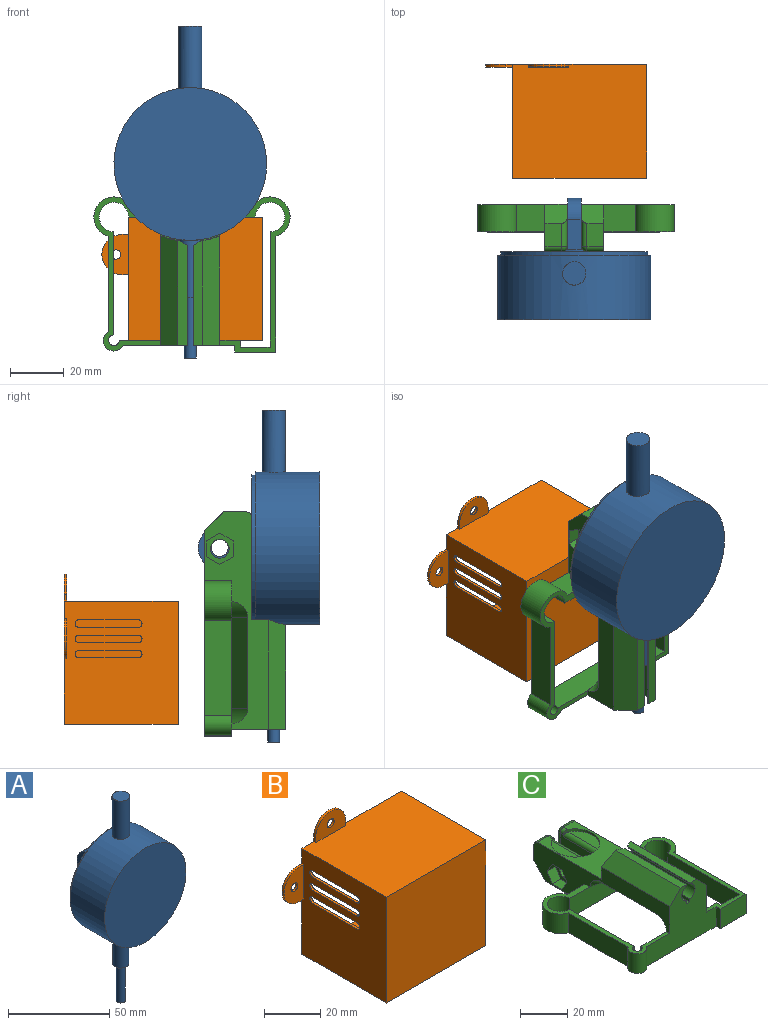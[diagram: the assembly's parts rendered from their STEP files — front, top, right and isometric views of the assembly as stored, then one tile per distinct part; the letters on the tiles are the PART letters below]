
ASSEMBLY  parts=3 mates=2
PART A: 31 faces, bbox 57x45.3x123.9 mm
  f0: cylinder r=28.5mm len=57mm, axis (0,1,0), area 4187.4mm2, adj f11,f12,f13,f15
  f1: plane 19x15.8mm, normal (1,0,0), area 242.2mm2, adj f3,f5,f6,f7,f8
  f2: plane 19x15.8mm, normal (-1,0,0), area 242.2mm2, adj f3,f5,f6,f7,f8
  f3: plane 20x20mm, normal (0,1,0), area 235.2mm2, adj f1,f2,f4,f5,f6
  f4: cylinder r=10mm len=20mm, axis (0,-1,0), area 62.8mm2, adj f3,f10
  f5: plane 11.1x5mm, normal (0,0,-1), area 55.5mm2, adj f1,f2,f3,f7
  f6: plane 11.1x5mm, normal (0,0,1), area 55.5mm2, adj f1,f2,f3,f7
  f7: cylinder r=7.9mm len=15.8mm, axis (1,0,0), area 124.1mm2, adj f1,f2,f5,f6
  f8: cylinder r=3.15mm len=6.3mm, axis (1,0,0), area 99mm2, adj f1,f2
  f9: cylinder r=27.4mm len=54.8mm, axis (0,1,0), area 223.8mm2, adj f10,f12
  f10: plane 54.8x54.8mm, normal (0,1,0), area 1980.8mm2, adj f4,f9,f21,f24,f27,f30
  f11: plane 57x57mm, normal (0,-1,0), area 2551.8mm2, adj f0
  f12: plane 57x57mm, normal (0,1,0), area 193.2mm2, adj f0,f9
  f13: cylinder r=4.35mm len=23.33mm, axis (0,0,-1), area 633.2mm2, adj f0,f14
  f14: plane 8.7x8.7mm, normal (0,0,1), area 59.4mm2, adj f13
  f15: cylinder r=4mm len=21.78mm, axis (0,0,1), area 543.9mm2, adj f0,f16
  f16: plane 8x8mm, normal (0,0,-1), area 35.1mm2, adj f15,f17
  f17: cylinder r=2.2mm len=22.4mm, axis (0,0,1), area 309.6mm2, adj f16,f18
  f18: plane 4.4x4.4mm, normal (0,0,-1), area 15.2mm2, adj f17
  f19: cone r=0mm half-angle=59deg, axis (0,1,0), area 3.7mm2, adj f20
  f20: cylinder r=1mm len=2mm, axis (0,1,0), area 4.7mm2, adj f19,f21
  f21: cone r=1mm half-angle=45deg, axis (0,1,0), area 18mm2, adj f10,f20
  f22: cone r=0mm half-angle=59deg, axis (0,1,0), area 3.7mm2, adj f23
  f23: cylinder r=1mm len=2mm, axis (0,1,0), area 4.7mm2, adj f22,f24
  f24: cone r=1mm half-angle=45deg, axis (0,1,0), area 18mm2, adj f10,f23
  f25: cone r=0mm half-angle=59deg, axis (0,1,0), area 3.7mm2, adj f26
  f26: cylinder r=1mm len=2mm, axis (0,1,0), area 4.7mm2, adj f25,f27
  f27: cone r=1mm half-angle=45deg, axis (0,1,0), area 18mm2, adj f10,f26
  f28: cone r=0mm half-angle=59deg, axis (0,1,0), area 3.7mm2, adj f29
  f29: cylinder r=1mm len=2mm, axis (0,1,0), area 4.7mm2, adj f28,f30
  f30: cone r=1mm half-angle=45deg, axis (0,1,0), area 18mm2, adj f10,f29
PART B: 33 faces, bbox 60x42.5x56 mm
  f0: plane 46x42.5mm, normal (-1,0,0), area 1735mm2, adj f1,f3,f4,f5,f11,f12,f15,f21
  f1: plane 50x42.5mm, normal (0,0,-1), area 2125mm2, adj f0,f2,f4,f5
  f2: plane 46x42.5mm, normal (1,0,0), area 1955mm2, adj f1,f3,f4,f5
  f3: plane 50x42.5mm, normal (0,0,1), area 2110mm2, adj f0,f2,f4,f5,f7,f9,f10
  f4: plane 50x46mm, normal (0,-1,0), area 2300mm2, adj f0,f1,f2,f3
  f5: plane 60x56mm, normal (0,1,0), area 420.5mm2, adj f0,f1,f2,f3,f6,f7,f8,f9
  f6: cylinder r=7.5mm len=15mm, axis (0,1,0), area 23.6mm2, adj f5,f7,f9,f10
  f7: plane 2.5x1mm, normal (-1,0,0), area 2.5mm2, adj f3,f5,f6,f10
  f8: cylinder r=1.75mm len=3.5mm, axis (0,1,0), area 11mm2, adj f5,f10
  f9: plane 2.5x1mm, normal (1,0,0), area 2.5mm2, adj f3,f5,f6,f10
  f10: plane 15x10mm, normal (0,-1,0), area 116.2mm2, adj f3,f6,f7,f8,f9
  f11: plane 2.5x1mm, normal (0,0,-1), area 2.5mm2, adj f0,f5,f13,f15
  f12: plane 2.5x1mm, normal (0,0,1), area 2.5mm2, adj f0,f5,f13,f15
  f13: cylinder r=7.5mm len=15mm, axis (0,1,0), area 23.6mm2, adj f5,f11,f12,f15
  f14: cylinder r=1.75mm len=3.5mm, axis (0,1,0), area 11mm2, adj f5,f15
  f15: plane 15x10mm, normal (0,-1,0), area 116.2mm2, adj f0,f11,f12,f13,f14
  f16: plane 44x41.5mm, normal (1,0,0), area 1621mm2, adj f5,f17,f19,f20,f21,f22,f23,f24
  f17: plane 48x41.5mm, normal (0,0,1), area 1992mm2, adj f5,f16,f18,f20
  f18: plane 44x41.5mm, normal (-1,0,0), area 1826mm2, adj f5,f17,f19,f20
  f19: plane 48x41.5mm, normal (0,0,-1), area 1992mm2, adj f5,f16,f18,f20
  f20: plane 48x44mm, normal (0,1,0), area 2112mm2, adj f16,f17,f18,f19
  f21: cylinder r=1.4mm len=2.8mm, axis (-1,0,0), area 4.4mm2, adj f0,f16,f22,f23
  f22: plane 22.2x1mm, normal (0,0,1), area 22.2mm2, adj f0,f16,f21,f24
  f23: plane 22.2x1mm, normal (0,0,-1), area 22.2mm2, adj f0,f16,f21,f24
  f24: cylinder r=1.4mm len=2.8mm, axis (-1,0,0), area 4.4mm2, adj f0,f16,f22,f23
  f25: cylinder r=1.4mm len=2.8mm, axis (-1,0,0), area 4.4mm2, adj f0,f16,f26,f27
  f26: plane 22.2x1mm, normal (0,0,1), area 22.2mm2, adj f0,f16,f25,f28
  f27: plane 22.2x1mm, normal (0,0,-1), area 22.2mm2, adj f0,f16,f25,f28
  f28: cylinder r=1.4mm len=2.8mm, axis (-1,0,0), area 4.4mm2, adj f0,f16,f26,f27
  f29: cylinder r=1.4mm len=2.8mm, axis (-1,0,0), area 4.4mm2, adj f0,f16,f30,f31
  f30: plane 22.2x1mm, normal (0,0,1), area 22.2mm2, adj f0,f16,f29,f32
  f31: plane 22.2x1mm, normal (0,0,-1), area 22.2mm2, adj f0,f16,f29,f32
  f32: cylinder r=1.4mm len=2.8mm, axis (-1,0,0), area 4.4mm2, adj f0,f16,f30,f31
PART C: 76 faces, bbox 76.5x86.9x34.9 mm
  f0: plane 39.62x4.22mm, normal (0,0,1), area 140.9mm2, adj f19,f47,f53,f57,f68
  f1: cylinder r=4mm len=36.74mm, axis (0,-1,0), area 387.4mm2, adj f19,f57,f66,f68
  f2: plane 18.33x5.6mm, normal (0,0,1), area 73.3mm2, adj f48,f64
  f3: plane 2.03x0.05mm, normal (0,0,1), area 0.1mm2, adj f48,f63
  f4: cylinder r=6mm len=11.77mm, axis (0.83,0,-0.55), area 45.5mm2, adj f5,f15,f55
  f5: plane 49.28x25.27mm, normal (0,0,-1), area 239.5mm2, adj f4,f7,f10,f15,f27,f31,f55,f56
  f6: plane 57.5x25mm, normal (0,0,1), area 221.4mm2, adj f15,f18,f19,f24,f25,f27,f28,f29
  f7: cylinder r=6mm len=11.77mm, axis (-0.83,0,-0.55), area 45.5mm2, adj f5,f10,f56
  f8: plane 57.91x26.25mm, normal (0,0,1), area 229.9mm2, adj f10,f17,f19,f20,f21,f22,f23,f26
  f9: plane 14.46x5.4mm, normal (0,1,0), area 78.1mm2, adj f12,f13,f36,f63
  f10: plane 82.6x25.49mm, normal (1,0,0), area 856.4mm2, adj f5,f7,f8,f11,f17,f19,f36,f38
  f11: plane 8.66x6.3mm, normal (0,1,0), area 54.5mm2, adj f10,f51,f59,f70
  f12: plane 20x15.66mm, normal (-1,0,0), area 240.3mm2, adj f9,f36,f38,f48,f51,f59,f64,f72
  f13: plane 20x15.66mm, normal (1,0,0), area 240.3mm2, adj f9,f16,f36,f48,f52,f58,f62,f75
  f14: plane 8.66x6.3mm, normal (0,1,0), area 54.5mm2, adj f15,f52,f58,f73
  f15: plane 82.6x25.49mm, normal (-1,0,0), area 804.8mm2, adj f4,f5,f6,f14,f19,f24,f36,f39
  f16: cylinder r=3.5mm len=7mm, axis (-1,0,0), area 72.6mm2, adj f13,f45
  f17: plane 11.83x10.16mm, normal (0,1,0), area 120.2mm2, adj f8,f10,f23,f36
  f18: cylinder r=4mm len=10.16mm, axis (0,0,-1), area 147.7mm2, adj f6,f19,f35,f36
  f19: plane 41.54x30.36mm, normal (0,-1,0), area 771.9mm2, adj f0,f1,f6,f8,f10,f15,f18,f20
  f20: plane 10.16x2.5mm, normal (-1,0,0), area 25.4mm2, adj f8,f19,f21,f36
  f21: plane 15.39x10.16mm, normal (0,-1,0), area 156.3mm2, adj f8,f20,f22,f36
  f22: plane 43.23x10.16mm, normal (1,0,0), area 439.2mm2, adj f8,f21,f23,f36
  f23: cylinder r=7.5mm len=14.67mm, axis (0,0,-1), area 306.2mm2, adj f8,f17,f22,f36
  f24: plane 10.58x10.16mm, normal (0,1,0), area 107.5mm2, adj f6,f15,f25,f36
  f25: cylinder r=7.5mm len=14.67mm, axis (0,0,-1), area 306.2mm2, adj f6,f24,f35,f36
  f26: plane 10.16x2.5mm, normal (1,0,0), area 25.4mm2, adj f8,f27,f34,f36
  f27: plane 45.25x10.16mm, normal (0,1,0), area 459.6mm2, adj f5,f6,f8,f26,f28,f36
  f28: cylinder r=2mm len=10.16mm, axis (0,0,-1), area 95.7mm2, adj f6,f27,f29,f36
  f29: plane 38.5x10.16mm, normal (1,0,0), area 391.1mm2, adj f6,f28,f30,f36
  f30: cylinder r=5.5mm len=11mm, axis (0,0,-1), area 263.3mm2, adj f6,f29,f31,f36
  f31: plane 47.25x10.16mm, normal (0,-1,0), area 480mm2, adj f5,f6,f8,f30,f32,f36
  f32: cylinder r=5.5mm len=11mm, axis (0,0,-1), area 263.3mm2, adj f8,f31,f33,f36
  f33: plane 43x10.16mm, normal (-1,0,0), area 436.8mm2, adj f8,f32,f34,f36
  f34: plane 11x10.16mm, normal (0,1,0), area 111.7mm2, adj f8,f26,f33,f36
  f35: plane 35.49x10.16mm, normal (-1,0,0), area 360.5mm2, adj f6,f18,f25,f36
  f36: plane 76.65x73.25mm, normal (0,0,-1), area 989.6mm2, adj f9,f10,f12,f13,f15,f17,f18,f19
  f37: plane 39.62x4.22mm, normal (0,0,1), area 140.9mm2, adj f19,f47,f54,f57,f69
  f38: cylinder r=3.5mm len=8.3mm, axis (-1,0,0), area 182.5mm2, adj f10,f12
  f39: plane 5.1x5mm, normal (0,0.87,0.5), area 29.4mm2, adj f15,f40,f44,f45
  f40: plane 5.1x5mm, normal (0,0.87,-0.5), area 29.4mm2, adj f15,f39,f41,f45
  f41: plane 5.89x5mm, normal (0,0,-1), area 29.4mm2, adj f15,f40,f42,f45
  f42: plane 5.1x5mm, normal (0,-0.87,-0.5), area 29.4mm2, adj f15,f41,f43,f45
  f43: plane 5.1x5mm, normal (0,-0.87,0.5), area 29.4mm2, adj f15,f42,f44,f45
  f44: plane 5.89x5mm, normal (0,0,1), area 29.4mm2, adj f15,f39,f43,f45
  f45: plane 11.78x10.2mm, normal (-1,0,0), area 51.6mm2, adj f16,f39,f40,f41,f42,f43,f44
  f46: plane 40.45x22mm, normal (0,0,1), area 523.7mm2, adj f10,f15,f47,f48,f70,f72,f73,f75
  f47: cylinder r=28.7mm len=22mm, axis (0,0,-1), area 146.1mm2, adj f0,f10,f15,f37,f46,f53,f54,f57
  f48: cylinder r=10.3mm len=20.6mm, axis (0,0,1), area 71.7mm2, adj f2,f3,f12,f13,f46,f49,f62,f63
  f49: plane 18.33x5.6mm, normal (0,0,1), area 73.3mm2, adj f48,f62
  f50: cylinder r=4mm len=36.74mm, axis (0,-1,0), area 387.4mm2, adj f19,f57,f67,f69
  f51: plane 9.14x7.84mm, normal (0,0.71,-0.71), area 81mm2, adj f10,f11,f12,f36,f59
  f52: plane 9.14x7.84mm, normal (0,0.71,-0.71), area 81mm2, adj f13,f14,f15,f36,f58
  f53: plane 41x6.43mm, normal (-0.71,0,0.71), area 356.3mm2, adj f0,f15,f19,f47
  f54: plane 41x6.43mm, normal (0.71,0,0.71), area 356.3mm2, adj f10,f19,f37,f47
  f55: plane 34x9mm, normal (-0.55,0,-0.83), area 367.8mm2, adj f4,f5,f15,f61
  f56: plane 34x9mm, normal (0.55,0,-0.83), area 367.8mm2, adj f5,f7,f10,f60
  f57: bspline ~11.84x11.21mm, area 67.5mm2, adj f0,f1,f37,f47,f50,f65,f66,f67
  f58: cylinder r=2mm len=10.66mm, axis (0,0,1), area 30.3mm2, adj f13,f14,f52,f74
  f59: cylinder r=2mm len=10.66mm, axis (0,0,-1), area 30.3mm2, adj f11,f12,f51,f71
  f60: cylinder r=6mm len=11.77mm, axis (-0.83,0,-0.55), area 45.5mm2, adj f5,f10,f56
  f61: cylinder r=6mm len=11.77mm, axis (0.83,0,-0.55), area 45.5mm2, adj f5,f15,f55
  f62: cylinder r=2mm len=19.45mm, axis (0,-1,0), area 58.3mm2, adj f13,f48,f49,f63
  f63: cylinder r=2mm len=7.92mm, axis (1,0,0), area 19.6mm2, adj f3,f9,f48,f62,f64
  f64: cylinder r=2mm len=19.45mm, axis (0,1,0), area 58.3mm2, adj f2,f12,f48,f63
  f65: plane 38.56x2.29mm, normal (0,0,1), area 76.4mm2, adj f19,f57,f66,f67
  f66: plane 38.31x1.62mm, normal (1,0,0), area 59.1mm2, adj f1,f19,f57,f65
  f67: plane 38.31x1.62mm, normal (-1,0,0), area 59.1mm2, adj f19,f50,f57,f65
  f68: plane 37.4x0.69mm, normal (1,0,0), area 25.1mm2, adj f0,f1,f19,f57
  f69: plane 37.4x0.69mm, normal (-1,0,0), area 25.2mm2, adj f19,f37,f50,f57
  f70: cylinder r=2mm len=6.3mm, axis (1,0,0), area 19.8mm2, adj f10,f11,f46,f71
  f71: sphere r=2mm, area 8.6mm2, adj f59,f70,f72
  f72: cylinder r=2mm len=2.59mm, axis (0,1,0), area 6.9mm2, adj f12,f46,f48,f71
  f73: cylinder r=2mm len=6.3mm, axis (1,0,0), area 19.8mm2, adj f14,f15,f46,f74
  f74: sphere r=2mm, area 4mm2, adj f58,f73,f75
  f75: cylinder r=2mm len=2.59mm, axis (0,-1,0), area 6.9mm2, adj f13,f46,f48,f74
PLACE A t=(23,-70,19.8)mm
PLACE B at identity
PLACE C rot(axis=(1,0,0),90deg) t=(23.62,-52.34,-23)mm
MATE slider C.f6 <-> B.f4  axis (0,-1,0) through (0,-62.5,0)mm
MATE slider C.f1 <-> A.f13  axis (0,0,-1) through (23,-78.15,-10.39)mm
